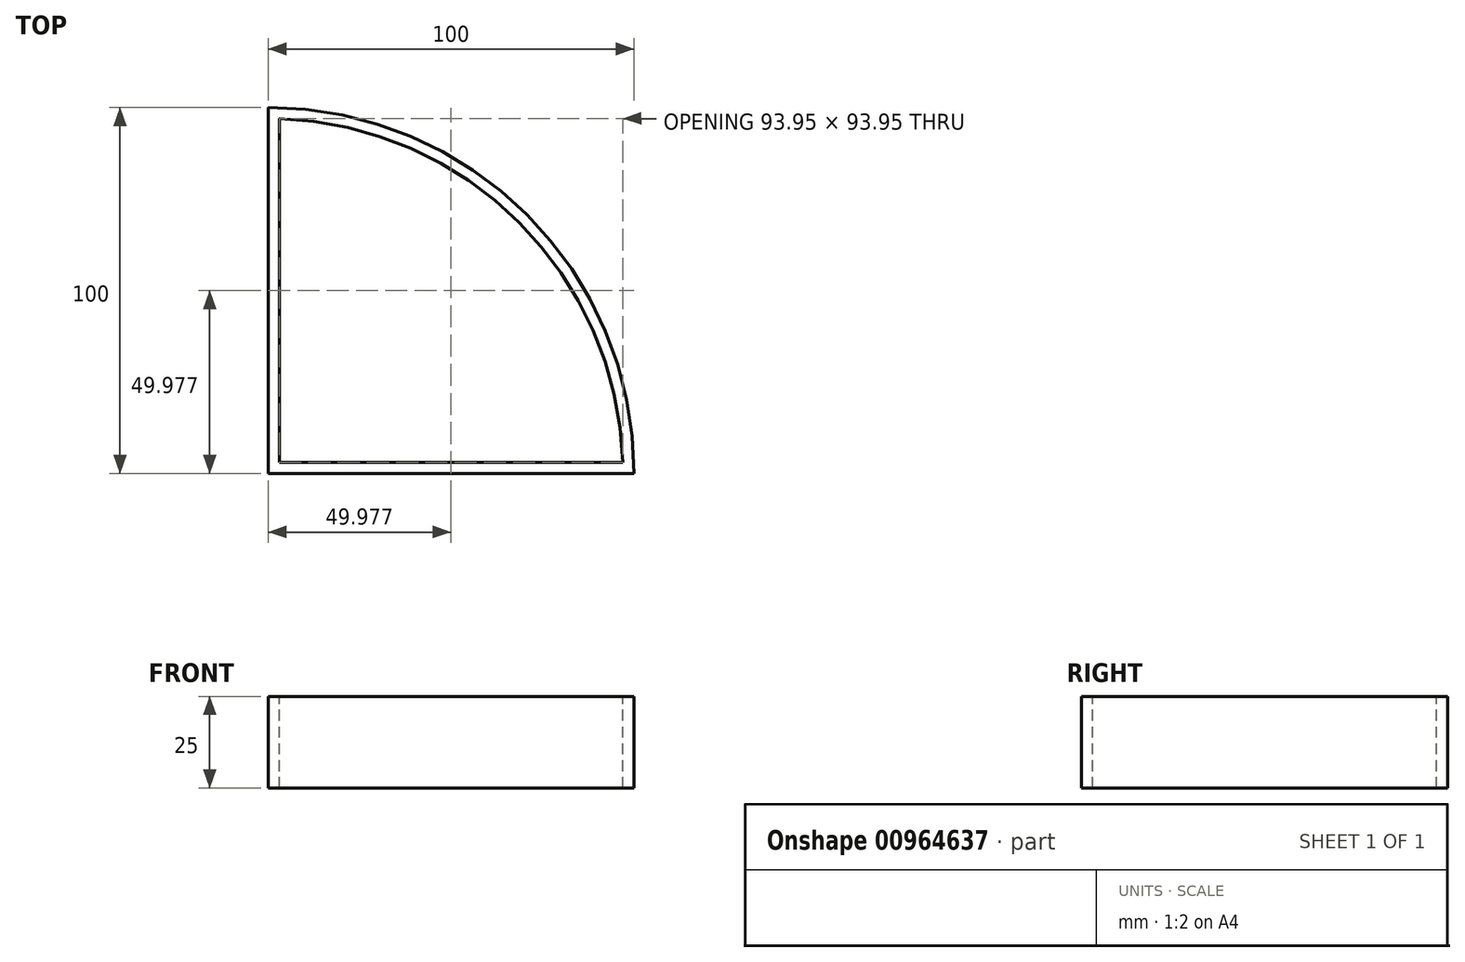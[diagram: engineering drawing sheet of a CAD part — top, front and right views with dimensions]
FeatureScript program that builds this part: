
annotation { "Feature Type Name" : "Feature", "Feature Type Description" : "" }
export const myFeature = defineFeature(function(context is Context, id is Id, definition is map)
    precondition{}
    {
        {
            var Q0;
            Q0=qCreatedBy(makeId("Top.planeOp"),FACE);
            var sketch = newSketch(context, id + "F0", { "sketchPlane" : qUnion([Q0])});
            skLineSegment(sketch, "E0.bottom", {"start": v(0, 0) * mm, "end": v(100, 0) * mm});
            skLineSegment(sketch, "E0.left", {"start": v(0, 0) * mm, "end": v(0, 100) * mm});
            skArc(sketch, "E1", {"start": v(0, 100) * mm, "mid": v(70.71, 70.71) * mm, "end": v(100, 0) * mm});
            skSolve(sketch);
        }
        {
            var Q0;
            Q0 = qSketchRegion(id + "F0", true);
            extrude(context, id + "F1", {"entities" : qUnion([Q0]), "oppositeDirection" : true, "depth" : 25 * mm, "offsetDistance" : 25 * mm});
        }
        {
            var Q0;
            Q0=makeQuery(id+"F1.opExtrude","CAP_FACE",FACE,{"disambiguationData":[OSD([sQuery(id+"F0.wireOp",EDGE,"E0.bottom"),sQuery(id+"F0.wireOp",EDGE,"E0.left"),sQuery(id+"F0.wireOp",EDGE,"E1")])],"isStart":true});
            var Q1;
            Q1=makeQuery(id+"F1.opExtrude","SWEPT_BODY",BODY,{"disambiguationData":[OSD([sQuery(id+"F0.wireOp",EDGE,"E0.bottom"),sQuery(id+"F0.wireOp",EDGE,"E0.left"),sQuery(id+"F0.wireOp",EDGE,"E1")])]});
            shell(context, id + "F2", {"entities" : qUnion([Q0]), "parts" : qUnion([Q1]), "thickness" : 3 * mm});
        }
        {
            var Q0;
            Q0=makeQuery(id+"F2.opShell","OFFSET_FACE",FACE,{"disambiguationData":[OSD([sQuery(id+"F0.wireOp",EDGE,"E0.bottom"),sQuery(id+"F0.wireOp",EDGE,"E0.left"),sQuery(id+"F0.wireOp",EDGE,"E1")])]});
            extrude(context, id + "F3", {"entities" : qUnion([Q0]), "operationType" : NewBodyOperationType.REMOVE, "surfaceOperationType" : NewSurfaceOperationType.ADD, "oppositeDirection" : true, "depth" : 25 * mm, "offsetDistance" : 25 * mm});
        }
    });
